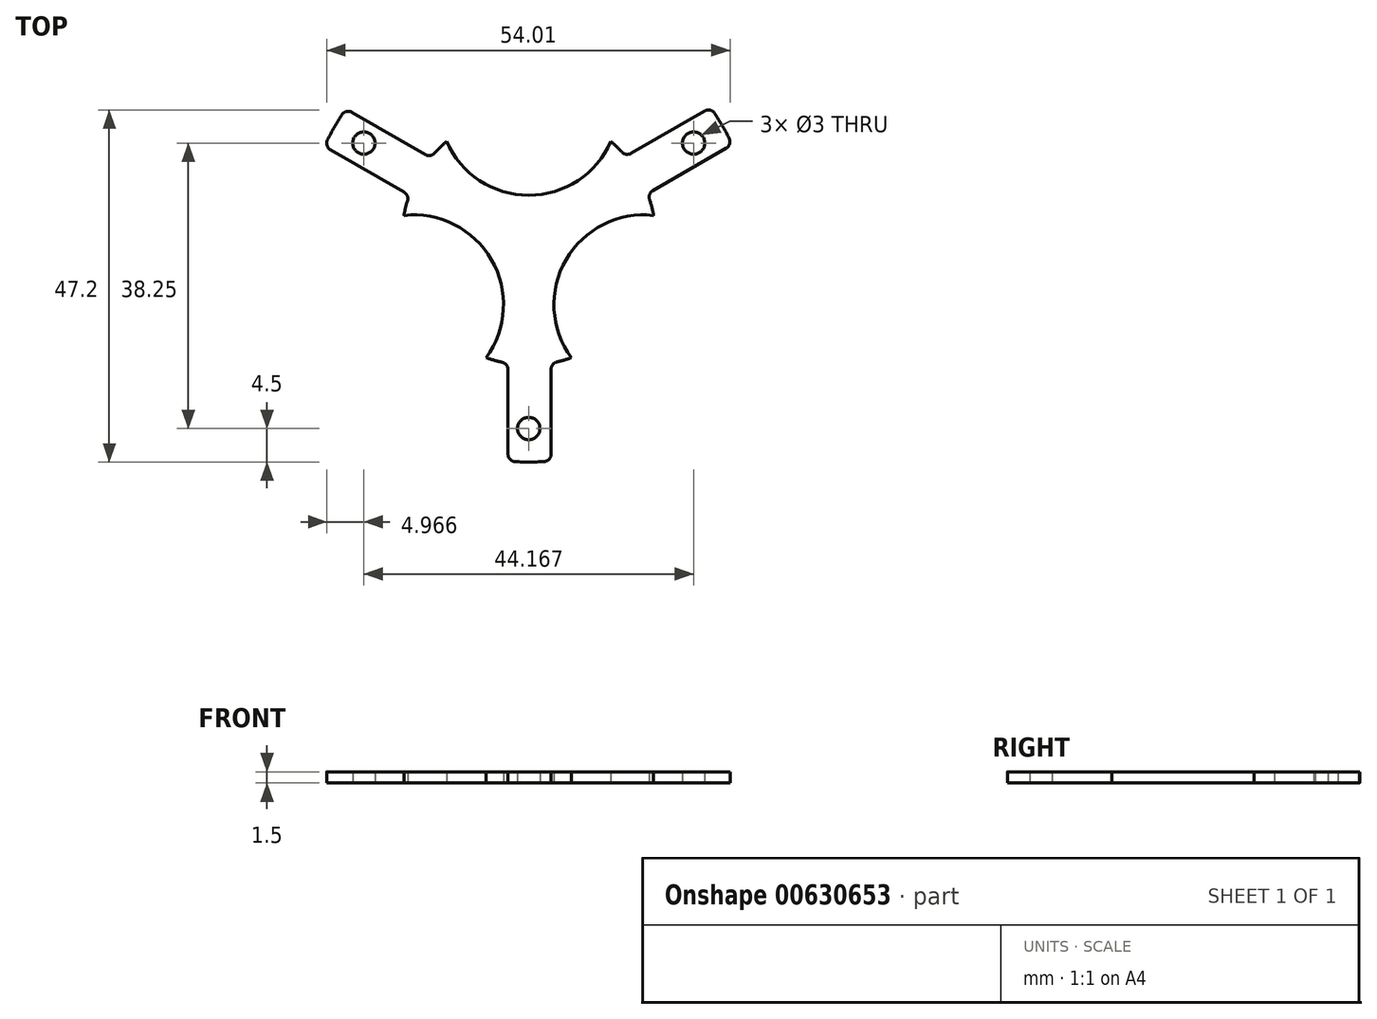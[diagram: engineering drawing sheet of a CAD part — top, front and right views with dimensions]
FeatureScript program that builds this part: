
annotation { "Feature Type Name" : "Feature", "Feature Type Description" : "" }
export const myFeature = defineFeature(function(context is Context, id is Id, definition is map)
    precondition{}
    {
        {
            var Q0;
            Q0=qCreatedBy(makeId("Top.planeOp"),FACE);
            var sketch = newSketch(context, id + "F0", { "sketchPlane" : qUnion([Q0])});
            skArc(sketch, "E0", {"start": v(-25.01, 16.56) * mm, "mid": v(-26.04, 14.9) * mm, "end": v(-26.95, 13.17) * mm});
            skArc(sketch, "E1", {"start": v(-11, 12.96) * mm, "mid": v(-11.83, 12.2) * mm, "end": v(-12.61, 11.4) * mm});
            skArc(sketch, "E2", {"start": v(-11, 12.96) * mm, "mid": v(0, 5.76) * mm, "end": v(11, 12.96) * mm});
            skLineSegment(sketch, "E3.0", {"start": v(3, -17.55) * mm, "end": v(3, -28.93) * mm});
            skLineSegment(sketch, "E4.0", {"start": v(-2.78, -17.6) * mm, "end": v(-2.78, -28.95) * mm});
            skArc(sketch, "E5.1.0", {"start": v(-5.72, -16) * mm, "mid": v(-4.99, -2.88) * mm, "end": v(-16.72, 3.05) * mm});
            skArc(sketch, "E5.2.0", {"start": v(16.72, 3.05) * mm, "mid": v(4.99, -2.88) * mm, "end": v(5.72, -16) * mm});
            skLineSegment(sketch, "E6.1.0", {"start": v(16.63, 6.4) * mm, "end": v(26.46, 12.07) * mm});
            skLineSegment(sketch, "E6.1.1", {"start": v(13.7, 11.37) * mm, "end": v(23.55, 17.06) * mm});
            skLineSegment(sketch, "E6.2.0", {"start": v(-13.85, 11.2) * mm, "end": v(-23.68, 16.88) * mm});
            skLineSegment(sketch, "E6.2.1", {"start": v(-16.7, 6.18) * mm, "end": v(-26.55, 11.87) * mm});
            skCircle(sketch, "E7", {"center": v(0, 0) * mm, "radius": 25.5 * mm, "construction": true});
            skCircle(sketch, "E8", {"center": v(0, -25.5) * mm, "radius": 1.5 * mm});
            skCircle(sketch, "E9.1.0", {"center": v(22.08, 12.75) * mm, "radius": 1.5 * mm});
            skCircle(sketch, "E9.2.0", {"center": v(-22.08, 12.75) * mm, "radius": 1.5 * mm});
            skArc(sketch, "E10.trimOffspring", {"start": v(-16.24, 5.02) * mm, "mid": v(-16.51, 4.04) * mm, "end": v(-16.72, 3.05) * mm});
            skArc(sketch, "E11.trimOffspring", {"start": v(12.47, 11.56) * mm, "mid": v(11.75, 12.28) * mm, "end": v(11, 12.96) * mm});
            skArc(sketch, "E12.trimOffspring", {"start": v(16.72, 3.05) * mm, "mid": v(16.49, 4.14) * mm, "end": v(16.18, 5.22) * mm});
            skArc(sketch, "E13.trimOffspring", {"start": v(3.78, -16.57) * mm, "mid": v(4.76, -16.32) * mm, "end": v(5.72, -16) * mm});
            skArc(sketch, "E14.trimOffspring", {"start": v(-5.72, -16) * mm, "mid": v(-4.66, -16.35) * mm, "end": v(-3.57, -16.62) * mm});
            skPoint(sketch, "E15.visualSharp", {"position": v(-13.14, 10.79) * mm});
            skArc(sketch, "E15.filletArc", {"start": v(-13.85, 11.2) * mm, "mid": v(-13.2, 11.08) * mm, "end": v(-12.61, 11.4) * mm});
            skPoint(sketch, "E16.visualSharp", {"position": v(13, 10.96) * mm});
            skArc(sketch, "E16.filletArc", {"start": v(12.47, 11.56) * mm, "mid": v(13.05, 11.25) * mm, "end": v(13.7, 11.37) * mm});
            skPoint(sketch, "E17.visualSharp", {"position": v(15.91, 5.98) * mm});
            skArc(sketch, "E17.filletArc", {"start": v(16.63, 6.4) * mm, "mid": v(16.2, 5.89) * mm, "end": v(16.18, 5.22) * mm});
            skPoint(sketch, "E18.visualSharp", {"position": v(3, -16.73) * mm});
            skArc(sketch, "E18.filletArc", {"start": v(3.78, -16.57) * mm, "mid": v(3.22, -16.93) * mm, "end": v(3, -17.55) * mm});
            skPoint(sketch, "E19.visualSharp", {"position": v(-2.78, -16.77) * mm});
            skArc(sketch, "E19.filletArc", {"start": v(-2.78, -17.6) * mm, "mid": v(-3, -16.97) * mm, "end": v(-3.57, -16.62) * mm});
            skPoint(sketch, "E20.visualSharp", {"position": v(-16, 5.77) * mm});
            skArc(sketch, "E20.filletArc", {"start": v(-16.24, 5.02) * mm, "mid": v(-16.27, 5.68) * mm, "end": v(-16.7, 6.18) * mm});
            skArc(sketch, "E21.trimOffspring", {"start": v(26.85, 13.38) * mm, "mid": v(25.92, 15.1) * mm, "end": v(24.88, 16.76) * mm});
            skArc(sketch, "E22.trimOffspring", {"start": v(-1.84, -29.94) * mm, "mid": v(0.12, -30) * mm, "end": v(2.07, -29.93) * mm});
            skPoint(sketch, "E23.newPointB", {"position": v(-24.83, 17.54) * mm});
            skArc(sketch, "E23.filletArc", {"start": v(-23.68, 16.88) * mm, "mid": v(-24.4, 16.98) * mm, "end": v(-25.01, 16.56) * mm});
            skPoint(sketch, "E24.newPointB", {"position": v(-27.48, 12.4) * mm});
            skArc(sketch, "E24.filletArc", {"start": v(-26.95, 13.17) * mm, "mid": v(-27.01, 12.44) * mm, "end": v(-26.55, 11.87) * mm});
            skPoint(sketch, "E25.newPointA", {"position": v(24.48, 17.6) * mm});
            skArc(sketch, "E25.filletArc", {"start": v(24.88, 16.76) * mm, "mid": v(24.28, 17.17) * mm, "end": v(23.55, 17.06) * mm});
            skPoint(sketch, "E26.newPointA", {"position": v(27.6, 12.74) * mm});
            skArc(sketch, "E26.filletArc", {"start": v(26.46, 12.07) * mm, "mid": v(26.91, 12.65) * mm, "end": v(26.85, 13.38) * mm});
            skPoint(sketch, "E27.newPointA", {"position": v(-2.78, -30.28) * mm});
            skArc(sketch, "E27.filletArc", {"start": v(-2.78, -28.95) * mm, "mid": v(-2.5, -29.63) * mm, "end": v(-1.84, -29.94) * mm});
            skPoint(sketch, "E28.newPointA", {"position": v(3, -30) * mm});
            skArc(sketch, "E28.filletArc", {"start": v(2.07, -29.93) * mm, "mid": v(2.73, -29.61) * mm, "end": v(3, -28.93) * mm});
            skSolve(sketch);
        }
        {
            var Q0;
            Q0=makeQuery(id+"F0.imprint","IMPRINT",FACE,{"disambiguationData":[TD([[makeQuery(id+"F0.imprint","IMPRINT",EDGE,{"derivedFrom":sQuery(id+"F0.wireOp",EDGE,"E0")}),1.0]])]});
            extrude(context, id + "F1", {"entities" : qUnion([Q0]), "depth" : 1.5 * mm, "offsetDistance" : 25 * mm});
        }
    });
